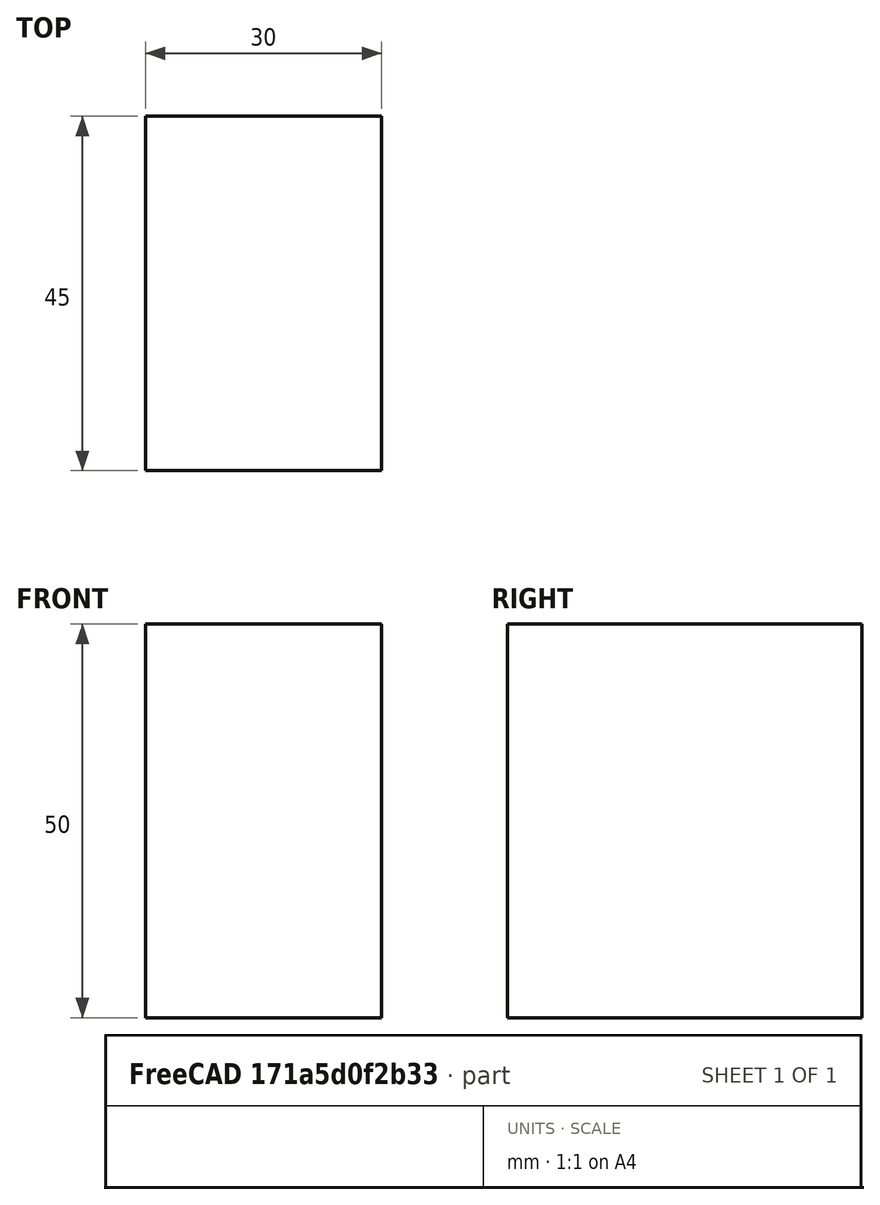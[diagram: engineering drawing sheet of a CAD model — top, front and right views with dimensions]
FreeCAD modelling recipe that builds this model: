
FCSTD DOCUMENT  (FreeCAD 1.0R39109 (Git))
Label: spacer
License: All rights reserved
LicenseURL: https://en.wikipedia.org/wiki/All_rights_reserved
objects: Sketcher::SketchObject×1, PartDesign::Pad×1, PartDesign::Body×1
note: 6 computed .brp shape members not serialized (recipe doc carries the construction recipe); baked Part::Feature solids carry a one-line shape summary decoded from their .brp

FEATURE [Sketcher::SketchObject] Sketch
  ArcFitTolerance = 1e-06
  AttachmentSupport = -> [XY_Plane]
  FullyConstrained = false
  MakeInternals = false
  MapMode = 5
  sketch-geometry (4):
    g0: LineSegment StartX=-13.8767 StartY=15.492 StartZ=0 EndX=-13.8767 EndY=-29.508 EndZ=0
    g1: LineSegment StartX=-13.8767 StartY=-29.508 StartZ=0 EndX=16.1233 EndY=-29.508 EndZ=0
    g2: LineSegment StartX=16.1233 StartY=-29.508 StartZ=0 EndX=16.1233 EndY=15.492 EndZ=0
    g3: LineSegment StartX=16.1233 StartY=15.492 StartZ=0 EndX=-13.8767 EndY=15.492 EndZ=0
  constraints (10):
    c: Coincident(g0,g1)
    c: Coincident(g1,g2)
    c: Coincident(g2,g3)
    c: Coincident(g3,g0)
    c: Vertical(g0)
    c: Vertical(g2)
    c: Horizontal(g1)
    c: Horizontal(g3)
    c: Distance(g0,g2) = 30
    c: Distance(g1,g3) = 45
FEATURE [PartDesign::Pad] Pad
  Direction = (0,0,1)
  Length = 50
  Length2 = 10
  Profile = -> Sketch
  ReferenceAxis = -> Sketch [N_Axis]
  Refine = true
  Suppressed = false
  Type = 0
FEATURE [PartDesign::Body] Body
  AllowCompound = false
  Group = -> [Sketch,Pad]
  Origin = -> Origin
  Tip = -> Pad
